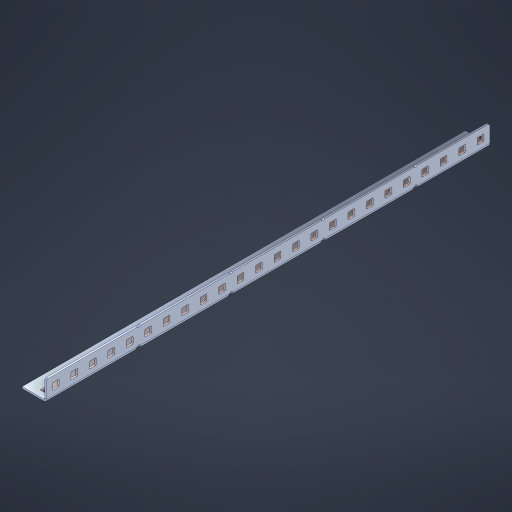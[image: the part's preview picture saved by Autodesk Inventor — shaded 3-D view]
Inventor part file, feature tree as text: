
AUTODESK INVENTOR PART (.ipt)
format: ipt  version: 2023 (Build 270158000, 158)  size: 827,904 bytes
history: native  units: in
note: dims shown in document units (in); Inventor stores cm internally (conversion verified against a paired STEP export)
features: other x53, extrude x47, sheet_metal_op x10, sketch x8, mirror x1, pattern_linear x1, chamfer x1
ambient origin geometry x8: Origin, YZ Plane, XZ Plane, XY Plane, X Axis, Y Axis, Z Axis, Center Point
bodies: Solid1 (feature_tree), Body (feature_tree)
feature tree (121):
  other  "Flange Pattern Plane"
  sheet_metal_op  "Flange Pattern"
  sheet_metal_op  "Body Pattern"
  other  "Arc Length"
  mirror  "Notch Mirror"
  pattern_linear  "Notch Pattern"  Spacing1=0.1875in  [1 undecoded]
  chamfer  "End Chamfer"
  extrude  "Half Cut"  Depth=0.0469in
  sketch  "Sketch1"  dims[d0=2.5in]
  other  "Plate1"
  sketch  "Sketch2"  dims[d1=12.0in]
  other  "Plate2"
  sheet_metal_op  "Bend1"
  sheet_metal_op  "Corner1"
  sketch  "Sketch3"  dims[d2=0.0469in]
  other  "Flange Pattern Sketch"
  sketch  "Sketch7"  dims[d3=0.0469in]
  other  "Srf1"
  other  "Srf2"
  sketch  "Sketch8"  dims[d4=0.0234in]
  sketch  "Sketch9"  dims[d5=0.0938in]
  other  "Srf91"
  sheet_metal_op  "Body Pattern Sketch"
  other  "Srf92"
  sketch  "Sketch13"  dims[d6=0.0469in]
  sketch  "Sketch14"  dims[d7=0.5in d8=90.0deg d9=0.0312in d10=0.1875in d11=0.0469in d12=0.0469in d16=0.182in d17=0.02in d18=0.0469in d19=0.0in d20=0.25in d21=0.25in d46=0.172in d47=1.0in d48=0.0in d49=0.182in d50=0.02in d51=0.25in d52=0.25in d53=0.0469in d54=0.0in d55=0.172in d56=1.0in d57=0.0in d60=9.4488in d62=0.5in d63=0.3937in d65=0.5in d85=0.1227in d86=0.1659in d88=0.04in d89=0.0469in d90=0.0in d91=0.04in d92=0.0491in d95=2.5in d96=0.04in d97=0.25in d98=45.0deg d101=0.0in d102=2.497in d131=0.5in d132=9.4488in d134=0.5in d139=0.5in]
  other  "Srf856"
  other  "Srf1310"
  other  "Srf1311"
  other  "Srf1312"
  other  "Srf1376"
  other  "Srf1377"
  other  "Srf1728"
  other  "Srf1755"
  other  "Srf1878"
  other  "Srf1879"
  other  "Srf1880"
  other  "Srf1881"
  other  "Srf1882"
  other  "Srf1883"
  other  "Srf1884"
  other  "Srf1885"
  other  "Srf1886"
  other  "Srf1887"
  other  "Srf1888"
  other  "Srf1889"
  other  "Srf1890"
  other  "Srf1891"
  other  "Srf1892"
  other  "Srf1893"
  other  "Srf1894"
  other  "Srf1895"
  other  "Srf1942"
  other  "Srf1943"
  other  "Srf1944"
  other  "Srf1945"
  other  "Srf1946"
  other  "Srf1947"
  other  "Srf1948"
  other  "Srf1949"
  other  "Srf1950"
  other  "Srf1951"
  other  "Srf1952"
  other  "Srf1953"
  other  "Srf1954"
  other  "Srf1955"
  other  "Srf1956"
  other  "Srf1957"
  other  "Srf1958"
  other  "Srf1959"
  sheet_metal_op  "Flange Stamp"
  sheet_metal_op  "Flange Circle"
  sheet_metal_op  "Body Stamp"
  sheet_metal_op  "Body Circle"
  sheet_metal_op  "Notch"
  extrude  "ExtrusionSrf2"  Depth=0.0469in
  extrude  "ExtrusionSrf92"  Depth=0.5in
  extrude  "ExtrusionSrf856"  Depth=0.02in
  extrude  "ExtrusionSrf1310"  Depth=0.0469in
  extrude  "ExtrusionSrf1311"  TaperAngle=0.0deg  [1 undecoded]
  extrude  "ExtrusionSrf1312"  Depth=0.5in
  extrude  "ExtrusionSrf1376"  Depth=0.5in
  extrude  "ExtrusionSrf1377"  Depth=0.5in
  extrude  "ExtrusionSrf1728"  Depth=0.5in TaperAngle=0.0deg
  extrude  "ExtrusionSrf1755"  Depth=0.5in
  extrude  "ExtrusionSrf1878"  Depth=0.02in
  extrude  "ExtrusionSrf1879"  Depth=0.5in
  extrude  "ExtrusionSrf1880"  Depth=0.5in
  extrude  "ExtrusionSrf1881"  Depth=0.0469in
  extrude  "ExtrusionSrf1882"  TaperAngle=0.0deg  [1 undecoded]
  extrude  "ExtrusionSrf1883"  Depth=0.5in
  extrude  "ExtrusionSrf1884"  Depth=0.5in TaperAngle=0.0deg
  extrude  "ExtrusionSrf1885"  Depth=0.5in
  extrude  "ExtrusionSrf1886"  Depth=0.5in
  extrude  "ExtrusionSrf1887"  Depth=0.5in
  extrude  "ExtrusionSrf1888"  Depth=0.5in
  extrude  "ExtrusionSrf1889"  Depth=0.5in
  extrude  "ExtrusionSrf1890"  Depth=0.0469in
  extrude  "ExtrusionSrf1891"  TaperAngle=0.0deg  [1 undecoded]
  extrude  "ExtrusionSrf1892"  Depth=0.5in
  extrude  "ExtrusionSrf1893"  Depth=0.5in
  extrude  "ExtrusionSrf1894"  Depth=0.5in
  extrude  "ExtrusionSrf1895"  Depth=0.5in TaperAngle=45.0deg
  extrude  "ExtrusionSrf1942"  TaperAngle=0.0deg  [1 undecoded]
  extrude  "ExtrusionSrf1943"  Depth=0.5in
  extrude  "ExtrusionSrf1944"  Depth=0.5in
  extrude  "ExtrusionSrf1945"  Depth=0.5in
  extrude  "ExtrusionSrf1946"  Depth=0.5in
  extrude  "ExtrusionSrf1947"  Depth=0.5in
  extrude  "ExtrusionSrf1948"  [1 undecoded]
  extrude  "ExtrusionSrf1949"  [1 undecoded]
  extrude  "ExtrusionSrf1950"  [1 undecoded]
  extrude  "ExtrusionSrf1951"  [1 undecoded]
  extrude  "ExtrusionSrf1952"  [1 undecoded]
  extrude  "ExtrusionSrf1953"  [1 undecoded]
  extrude  "ExtrusionSrf1954"  [1 undecoded]
  extrude  "ExtrusionSrf1955"  [1 undecoded]
  extrude  "ExtrusionSrf1956"  [1 undecoded]
  extrude  "ExtrusionSrf1957"  [1 undecoded]
  extrude  "ExtrusionSrf1958"  [1 undecoded]
  extrude  "ExtrusionSrf1959"  [1 undecoded]
note: 17 required parameter values undecoded (feature->parameter linkage not recoverable at this tier; creation-order binding heuristic only, values carry confidence <= 0.55)
